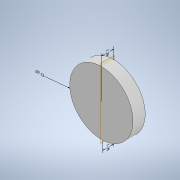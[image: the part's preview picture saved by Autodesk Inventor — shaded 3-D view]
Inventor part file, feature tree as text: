
AUTODESK INVENTOR PART (.ipt)
format: ipt  version: 2021.1 (Build 251245000, 245)  size: 841,728 bytes
history: native  units: in
note: dims shown in document units (in); Inventor stores cm internally (conversion verified against a paired STEP export)
features: other x4, extrude x3, sketch x2
ambient origin geometry x8: Origin, YZ Plane, XZ Plane, XY Plane, X Axis, Y Axis, Z Axis, Center Point
bodies: Solid1 (feature_tree)
feature tree (9):
  other  "Annotations"
  sketch  "Sketch1"  dims[d0=6.875in d1=0.125in]
  extrude  "Extrusion1"  Depth=0.125in
  extrude  "Extrusion2"  Depth=1.25in TaperAngle=0.0deg
  extrude  "Extrusion3"  Depth=0.05in TaperAngle=0.0deg
  sketch  "Sketch2"  dims[d2=0.125in d3=0.0in d4=1.25in d5=0.0in d6=0.05in d7=0.0in d10=1.2742in d11=7.125in d12=1.375in d13=1.25in]
  other  "Diameter Dimension 1"
  other  "Linear Dimension 1"
  other  "Linear Dimension 2"
